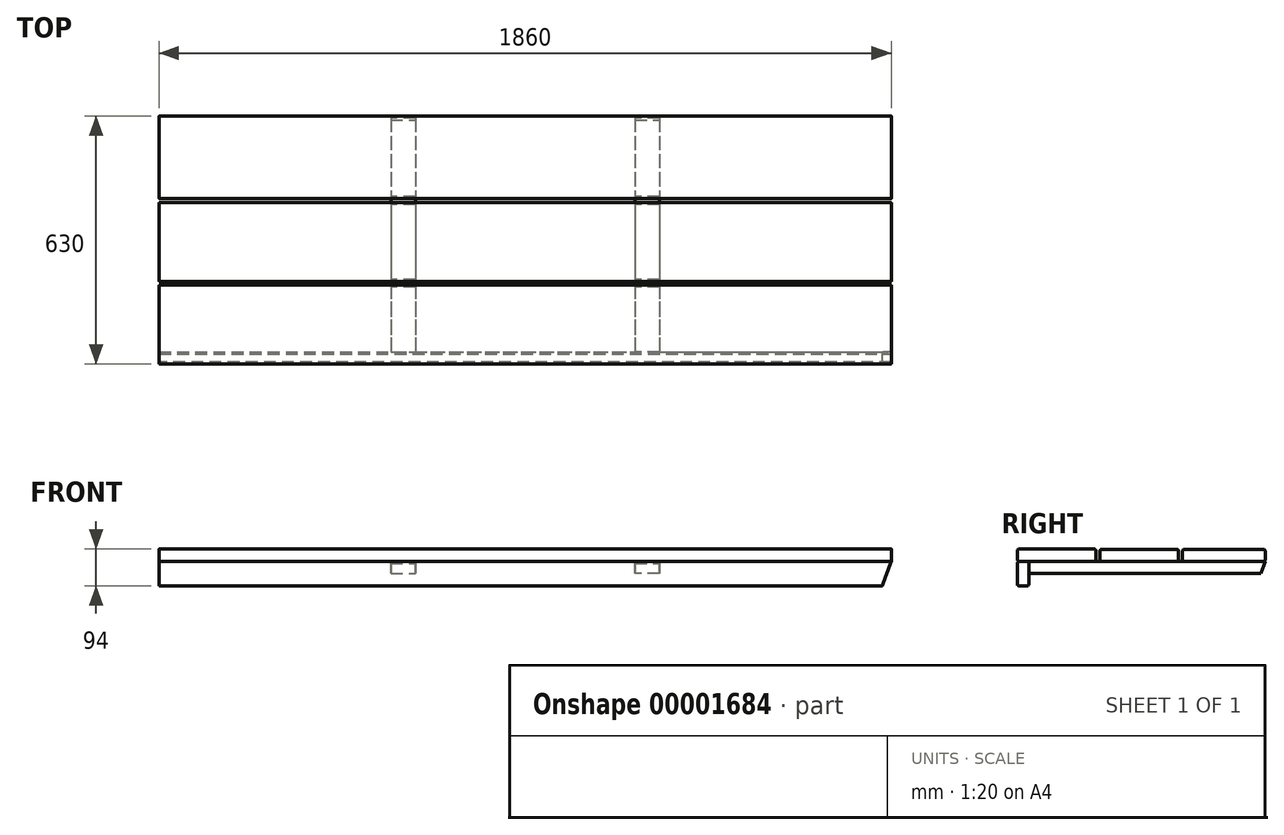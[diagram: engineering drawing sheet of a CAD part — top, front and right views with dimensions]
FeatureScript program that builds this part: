
annotation { "Feature Type Name" : "Feature", "Feature Type Description" : "" }
export const myFeature = defineFeature(function(context is Context, id is Id, definition is map)
    precondition{}
    {
        {
            var Q0;
            Q0=qCreatedBy(makeId("Right.planeOp"),FACE);
            var sketch = newSketch(context, id + "F0", { "sketchPlane" : qUnion([Q0])});
            skLineSegment(sketch, "E0.bottom", {"start": v(5, 0) * mm, "end": v(195, 0) * mm});
            skLineSegment(sketch, "E0.top", {"start": v(5, 32) * mm, "end": v(195, 32) * mm});
            skLineSegment(sketch, "E0.left", {"start": v(0, 5) * mm, "end": v(0, 27) * mm});
            skLineSegment(sketch, "E0.right", {"start": v(200, 5) * mm, "end": v(200, 27) * mm});
            skPoint(sketch, "E1.visualSharp", {"position": v(0, 32) * mm});
            skArc(sketch, "E1.filletArc", {"start": v(5, 32) * mm, "mid": v(1.46, 30.54) * mm, "end": v(0, 27) * mm});
            skPoint(sketch, "E2.visualSharp", {"position": v(200, 32) * mm});
            skArc(sketch, "E2.filletArc", {"start": v(200, 27) * mm, "mid": v(198.54, 30.54) * mm, "end": v(195, 32) * mm});
            skPoint(sketch, "E3.visualSharp", {"position": v(200, 0) * mm});
            skArc(sketch, "E3.filletArc", {"start": v(195, 0) * mm, "mid": v(198.54, 1.46) * mm, "end": v(200, 5) * mm});
            skPoint(sketch, "E4.visualSharp", {"position": v(0, 0) * mm});
            skArc(sketch, "E4.filletArc", {"start": v(0, 5) * mm, "mid": v(1.46, 1.46) * mm, "end": v(5, 0) * mm});
            skLineSegment(sketch, "E5.bottom", {"start": v(215, 0) * mm, "end": v(405, 0) * mm});
            skLineSegment(sketch, "E5.top", {"start": v(215, 31.25) * mm, "end": v(405, 31.25) * mm});
            skLineSegment(sketch, "E5.left", {"start": v(210, 5) * mm, "end": v(210, 26.25) * mm});
            skLineSegment(sketch, "E5.right", {"start": v(410, 5) * mm, "end": v(410, 26.25) * mm});
            skPoint(sketch, "E6.visualSharp", {"position": v(210, 31.25) * mm});
            skArc(sketch, "E6.filletArc", {"start": v(215, 31.25) * mm, "mid": v(211.46, 29.78) * mm, "end": v(210, 26.25) * mm});
            skPoint(sketch, "E7.visualSharp", {"position": v(410, 31.25) * mm});
            skArc(sketch, "E7.filletArc", {"start": v(410, 26.25) * mm, "mid": v(408.54, 29.78) * mm, "end": v(405, 31.25) * mm});
            skPoint(sketch, "E8.visualSharp", {"position": v(410, 0) * mm});
            skArc(sketch, "E8.filletArc", {"start": v(405, 0) * mm, "mid": v(408.54, 1.46) * mm, "end": v(410, 5) * mm});
            skPoint(sketch, "E9.visualSharp", {"position": v(210, 0) * mm});
            skArc(sketch, "E9.filletArc", {"start": v(210, 5) * mm, "mid": v(211.46, 1.46) * mm, "end": v(215, 0) * mm});
            skLineSegment(sketch, "E10.bottom", {"start": v(425, 0) * mm, "end": v(625, 0) * mm});
            skLineSegment(sketch, "E10.top", {"start": v(425, 31.25) * mm, "end": v(625, 31.25) * mm});
            skLineSegment(sketch, "E10.left", {"start": v(420, 5) * mm, "end": v(420, 26.25) * mm});
            skLineSegment(sketch, "E10.right", {"start": v(630, 5) * mm, "end": v(630, 26.25) * mm});
            skPoint(sketch, "E11.visualSharp", {"position": v(420, 31.25) * mm});
            skArc(sketch, "E11.filletArc", {"start": v(425, 31.25) * mm, "mid": v(421.46, 29.78) * mm, "end": v(420, 26.25) * mm});
            skPoint(sketch, "E12.visualSharp", {"position": v(420, 0) * mm});
            skArc(sketch, "E12.filletArc", {"start": v(420, 5) * mm, "mid": v(421.46, 1.46) * mm, "end": v(425, 0) * mm});
            skPoint(sketch, "E13.visualSharp", {"position": v(630, 0) * mm});
            skArc(sketch, "E13.filletArc", {"start": v(625, 0) * mm, "mid": v(628.54, 1.46) * mm, "end": v(630, 5) * mm});
            skPoint(sketch, "E14.visualSharp", {"position": v(630, 31.25) * mm});
            skArc(sketch, "E14.filletArc", {"start": v(630, 26.25) * mm, "mid": v(628.54, 29.78) * mm, "end": v(625, 31.25) * mm});
            skSolve(sketch);
        }
        {
            var Q0;
            Q0=makeQuery(id+"F0.imprint","IMPRINT",FACE,{"disambiguationData":[TD([[makeQuery(id+"F0.imprint","IMPRINT",EDGE,{"derivedFrom":sQuery(id+"F0.wireOp",EDGE,"E0.bottom")}),1.0]])]});
            var Q1;
            Q1=makeQuery(id+"F0.imprint","IMPRINT",FACE,{"disambiguationData":[TD([[makeQuery(id+"F0.imprint","IMPRINT",EDGE,{"derivedFrom":sQuery(id+"F0.wireOp",EDGE,"E5.bottom")}),1.0]])]});
            var Q2;
            Q2=makeQuery(id+"F0.imprint","IMPRINT",FACE,{"disambiguationData":[TD([[makeQuery(id+"F0.imprint","IMPRINT",EDGE,{"derivedFrom":sQuery(id+"F0.wireOp",EDGE,"E10.bottom")}),1.0]])]});
            extrude(context, id + "F1", {"entities" : qUnion([Q0, Q1, Q2]), "depth" : 1860 * mm});
        }
        {
            var Q0;
            Q0=makeQuery(id+"F1.opExtrude","CAP_FACE",FACE,{"disambiguationData":[OSD([sQuery(id+"F0.wireOp",EDGE,"E0.bottom"),sQuery(id+"F0.wireOp",EDGE,"E0.top"),sQuery(id+"F0.wireOp",EDGE,"E0.left"),sQuery(id+"F0.wireOp",EDGE,"E0.right"),sQuery(id+"F0.wireOp",EDGE,"E1.filletArc"),sQuery(id+"F0.wireOp",EDGE,"E2.filletArc"),sQuery(id+"F0.wireOp",EDGE,"E3.filletArc"),sQuery(id+"F0.wireOp",EDGE,"E4.filletArc")])],"isStart":false});
            var sketch = newSketch(context, id + "F2", { "sketchPlane" : qUnion([Q0])});
            skLineSegment(sketch, "E15.bottom", {"start": v(5, -62) * mm, "end": v(25, -62) * mm});
            skLineSegment(sketch, "E15.top", {"start": v(5, 0) * mm, "end": v(25, 0) * mm});
            skLineSegment(sketch, "E15.left", {"start": v(0, -57) * mm, "end": v(0, -5) * mm});
            skLineSegment(sketch, "E15.right", {"start": v(30, -57) * mm, "end": v(30, -5) * mm});
            skPoint(sketch, "E16.visualSharp", {"position": v(0, 0) * mm});
            skArc(sketch, "E16.filletArc", {"start": v(5, 0) * mm, "mid": v(1.46, -1.46) * mm, "end": v(0, -5) * mm});
            skPoint(sketch, "E17.visualSharp", {"position": v(30, 0) * mm});
            skArc(sketch, "E17.filletArc", {"start": v(30, -5) * mm, "mid": v(28.54, -1.46) * mm, "end": v(25, 0) * mm});
            skPoint(sketch, "E18.visualSharp", {"position": v(30, -62) * mm});
            skArc(sketch, "E18.filletArc", {"start": v(25, -62) * mm, "mid": v(28.54, -60.54) * mm, "end": v(30, -57) * mm});
            skPoint(sketch, "E19.visualSharp", {"position": v(0, -62) * mm});
            skArc(sketch, "E19.filletArc", {"start": v(0, -57) * mm, "mid": v(1.46, -60.54) * mm, "end": v(5, -62) * mm});
            skSolve(sketch);
        }
        {
            var Q0;
            Q0=makeQuery(id+"F2.imprint","IMPRINT",FACE,{"disambiguationData":[TD([[makeQuery(id+"F2.imprint","IMPRINT",EDGE,{"derivedFrom":sQuery(id+"F2.wireOp",EDGE,"E15.bottom")}),1.0]])]});
            var Q1;
            Q1=makeQuery(id+"F1.opExtrude","CAP_FACE",FACE,{"disambiguationData":[OSD([sQuery(id+"F0.wireOp",EDGE,"E0.bottom"),sQuery(id+"F0.wireOp",EDGE,"E0.top"),sQuery(id+"F0.wireOp",EDGE,"E0.left"),sQuery(id+"F0.wireOp",EDGE,"E0.right"),sQuery(id+"F0.wireOp",EDGE,"E1.filletArc"),sQuery(id+"F0.wireOp",EDGE,"E2.filletArc"),sQuery(id+"F0.wireOp",EDGE,"E3.filletArc"),sQuery(id+"F0.wireOp",EDGE,"E4.filletArc")])],"isStart":true});
            extrude(context, id + "F3", {"entities" : qUnion([Q0]), "operationType" : NewBodyOperationType.ADD, "endBound" : BoundingType.UP_TO_SURFACE, "oppositeDirection" : true, "endBoundEntityFace" : qUnion([Q1]), "depth" : 25 * mm});
        }
        {
            var Q0;
            Q0=makeQuery(id+"F1.opExtrude","CAP_FACE",FACE,{"disambiguationData":[OSD([sQuery(id+"F0.wireOp",EDGE,"E10.bottom"),sQuery(id+"F0.wireOp",EDGE,"E10.top"),sQuery(id+"F0.wireOp",EDGE,"E10.left"),sQuery(id+"F0.wireOp",EDGE,"E10.right"),sQuery(id+"F0.wireOp",EDGE,"E11.filletArc"),sQuery(id+"F0.wireOp",EDGE,"E12.filletArc"),sQuery(id+"F0.wireOp",EDGE,"E13.filletArc"),sQuery(id+"F0.wireOp",EDGE,"E14.filletArc")])],"isStart":false});
            cPlane(context, id + "F4", {"entities" : qUnion([Q0]), "cplaneType" : CPlaneType.OFFSET, "offset" : 930 * mm, "oppositeDirection" : true, "width" : 150 * mm, "height" : 150 * mm});
        }
        {
            var Q0;
            Q0=makeQuery(id+"F3.opExtrude","SWEPT_FACE",FACE,{"disambiguationData":[OSD([sQuery(id+"F2.wireOp",EDGE,"E15.right")])]});
            var sketch = newSketch(context, id + "F5", { "sketchPlane" : qUnion([Q0])});
            skLineSegment(sketch, "E20.bottom", {"start": v(-1271, -30) * mm, "end": v(-1209, -30) * mm});
            skLineSegment(sketch, "E20.top", {"start": v(-1271, 0) * mm, "end": v(-1209, 0) * mm});
            skLineSegment(sketch, "E20.left", {"start": v(-1271, -30) * mm, "end": v(-1271, 0) * mm});
            skLineSegment(sketch, "E20.right", {"start": v(-1209, -30) * mm, "end": v(-1209, 0) * mm});
            skLineSegment(sketch, "E21", {"start": v(-1240, -30) * mm, "end": v(-1240, 0) * mm});
            skLineSegment(sketch, "E22.0.MirrorCS", {"start": v(-589, -30) * mm, "end": v(-651, -30) * mm});
            skLineSegment(sketch, "E22.1.MirrorCS", {"start": v(-651, -30) * mm, "end": v(-651, 0) * mm});
            skLineSegment(sketch, "E22.2.MirrorCS", {"start": v(-620, -30) * mm, "end": v(-620, 0) * mm});
            skLineSegment(sketch, "E22.3.MirrorCS", {"start": v(-589, 0) * mm, "end": v(-651, 0) * mm});
            skLineSegment(sketch, "E22.4.MirrorCS", {"start": v(-589, -30) * mm, "end": v(-589, 0) * mm});
            skSolve(sketch);
        }
        {
            var Q0;
            {var subQ3=sQuery(id+"F5.wireOp",EDGE,"E20.left");var subQ6=sQuery(id+"F5.wireOp",EDGE,"E20.top");var subQ9=makeQuery(id+"F5.imprint","INTERSECT",VERTEX,{"derivedFrom":[subQ6,subQ3]});var subQ10=sQuery(id+"F5.wireOp",EDGE,"E20.right");var subQ13=makeQuery(id+"F5.imprint","INTERSECT",VERTEX,{"derivedFrom":[subQ6,subQ10]});var subQ14=sQuery(id+"F5.wireOp",EDGE,"E22.2.MirrorCS");var subQ16=sQuery(id+"F5.wireOp",EDGE,"E22.1.MirrorCS");var subQ19=sQuery(id+"F5.wireOp",EDGE,"E22.3.MirrorCS");var subQ20=makeQuery(id+"F5.imprint","INTERSECT",VERTEX,{"derivedFrom":[subQ14,subQ19]});var subQ21=makeQuery(id+"F5.imprint","INTERSECT",VERTEX,{"derivedFrom":[subQ16,subQ19]});var subQ23=sQuery(id+"F5.wireOp",EDGE,"E22.4.MirrorCS");var subQ27=sQuery(id+"F5.wireOp",EDGE,"E20.bottom");var subQ30=makeQuery(id+"F5.imprint","INTERSECT",VERTEX,{"derivedFrom":[subQ27,subQ3]});var subQ31=makeQuery(id+"F5.imprint","INTERSECT",VERTEX,{"derivedFrom":[subQ27,subQ10]});var subQ32=sQuery(id+"F5.wireOp",EDGE,"E22.0.MirrorCS");var subQ33=makeQuery(id+"F5.imprint","INTERSECT",VERTEX,{"derivedFrom":[subQ32,subQ23]});var subQ36=makeQuery(id+"F5.imprint","INTERSECT",VERTEX,{"derivedFrom":[subQ32,subQ16]});Q0=qUnion([makeQuery(id+"F5.imprint","IMPRINT",FACE,{"disambiguationData":[TD([[makeQuery(id+"F5.imprint","IMPRINT",EDGE,{"disambiguationData":[TD([[subQ9,-1.0]])],"derivedFrom":subQ6}),-1.0]])]}),makeQuery(id+"F5.imprint","IMPRINT",FACE,{"disambiguationData":[TD([[makeQuery(id+"F5.imprint","IMPRINT",EDGE,{"disambiguationData":[TD([[subQ13,1.0]])],"derivedFrom":subQ6}),-1.0]])]}),makeQuery(id+"F5.imprint","IMPRINT",FACE,{"disambiguationData":[TD([[makeQuery(id+"F5.imprint","IMPRINT",EDGE,{"disambiguationData":[TD([[subQ21,1.0]])],"derivedFrom":subQ19}),1.0]])]}),makeQuery(id+"F5.imprint","IMPRINT",FACE,{"disambiguationData":[TD([[makeQuery(id+"F5.imprint","IMPRINT",EDGE,{"disambiguationData":[TD([[subQ20,1.0]])],"derivedFrom":subQ19}),1.0]])]}),makeQuery(id+"F5.imprint","IMPRINT",FACE,{"disambiguationData":[TD([[makeQuery(id+"F5.imprint","IMPRINT",EDGE,{"disambiguationData":[TD([[subQ30,-1.0]])],"derivedFrom":subQ27}),1.0]])]}),makeQuery(id+"F5.imprint","IMPRINT",FACE,{"disambiguationData":[TD([[makeQuery(id+"F5.imprint","IMPRINT",EDGE,{"disambiguationData":[TD([[subQ31,1.0]])],"derivedFrom":subQ27}),1.0]])]}),makeQuery(id+"F5.imprint","IMPRINT",FACE,{"disambiguationData":[TD([[makeQuery(id+"F5.imprint","IMPRINT",EDGE,{"disambiguationData":[TD([[subQ33,-1.0]])],"derivedFrom":subQ32}),-1.0]])]}),makeQuery(id+"F5.imprint","IMPRINT",FACE,{"disambiguationData":[TD([[makeQuery(id+"F5.imprint","IMPRINT",EDGE,{"disambiguationData":[TD([[subQ36,1.0]])],"derivedFrom":subQ32}),-1.0]])]})]);}
            extrude(context, id + "F6", {"entities" : qUnion([Q0]), "operationType" : NewBodyOperationType.ADD, "depth" : 750 * mm});
        }
        {
            var Q0;
            Q0=makeQuery(id+"F6.opExtrude","SWEPT_FACE",FACE,{"disambiguationData":[OSD([sQuery(id+"F5.wireOp",EDGE,"E20.left")])]});
            var sketch = newSketch(context, id + "F7", { "sketchPlane" : qUnion([Q0])});
            skLineSegment(sketch, "E23", {"start": v(630, 0) * mm, "end": v(619.08, -30) * mm});
            skSolve(sketch);
        }
        {
            var Q0;
            Q0 = qSketchRegion(id + "F7", true);
            var Q1;
            {var subQ3=sQuery(id+"F7.wireOp",EDGE,"E23");Q1=makeQuery(id+"F7.imprint","IMPRINT",FACE,{"disambiguationData":[TD([[makeQuery(id+"F7.imprint","IMPRINT",EDGE,{"derivedFrom":subQ3}),1.0]])]});}
            extrude(context, id + "F8", {"entities" : qUnion([Q0, Q1]), "operationType" : NewBodyOperationType.REMOVE, "endBound" : BoundingType.THROUGH_ALL, "oppositeDirection" : true, "depth" : 25 * mm});
        }
        {
            var Q0;
            Q0=makeQuery(id+"F3.opExtrude","SWEPT_FACE",FACE,{"disambiguationData":[OSD([sQuery(id+"F2.wireOp",EDGE,"E15.right")])]});
            var sketch = newSketch(context, id + "F9", { "sketchPlane" : qUnion([Q0])});
            skLineSegment(sketch, "E24", {"start": v(-1860, 0) * mm, "end": v(-1837.43, -62) * mm});
            skLineSegment(sketch, "E25", {"start": v(-1860, 0) * mm, "end": v(-1860, 0) * mm});
            skLineSegment(sketch, "E26", {"start": v(-1860, 0) * mm, "end": v(-1860, -62) * mm});
            skLineSegment(sketch, "E27", {"start": v(-1837.43, -62) * mm, "end": v(-1860, -62) * mm});
            skSolve(sketch);
        }
        {
            var Q0;
            Q0 = qSketchRegion(id + "F9", true);
            extrude(context, id + "F10", {"entities" : qUnion([Q0]), "operationType" : NewBodyOperationType.REMOVE, "endBound" : BoundingType.THROUGH_ALL, "oppositeDirection" : true, "depth" : 25 * mm});
        }
    });
